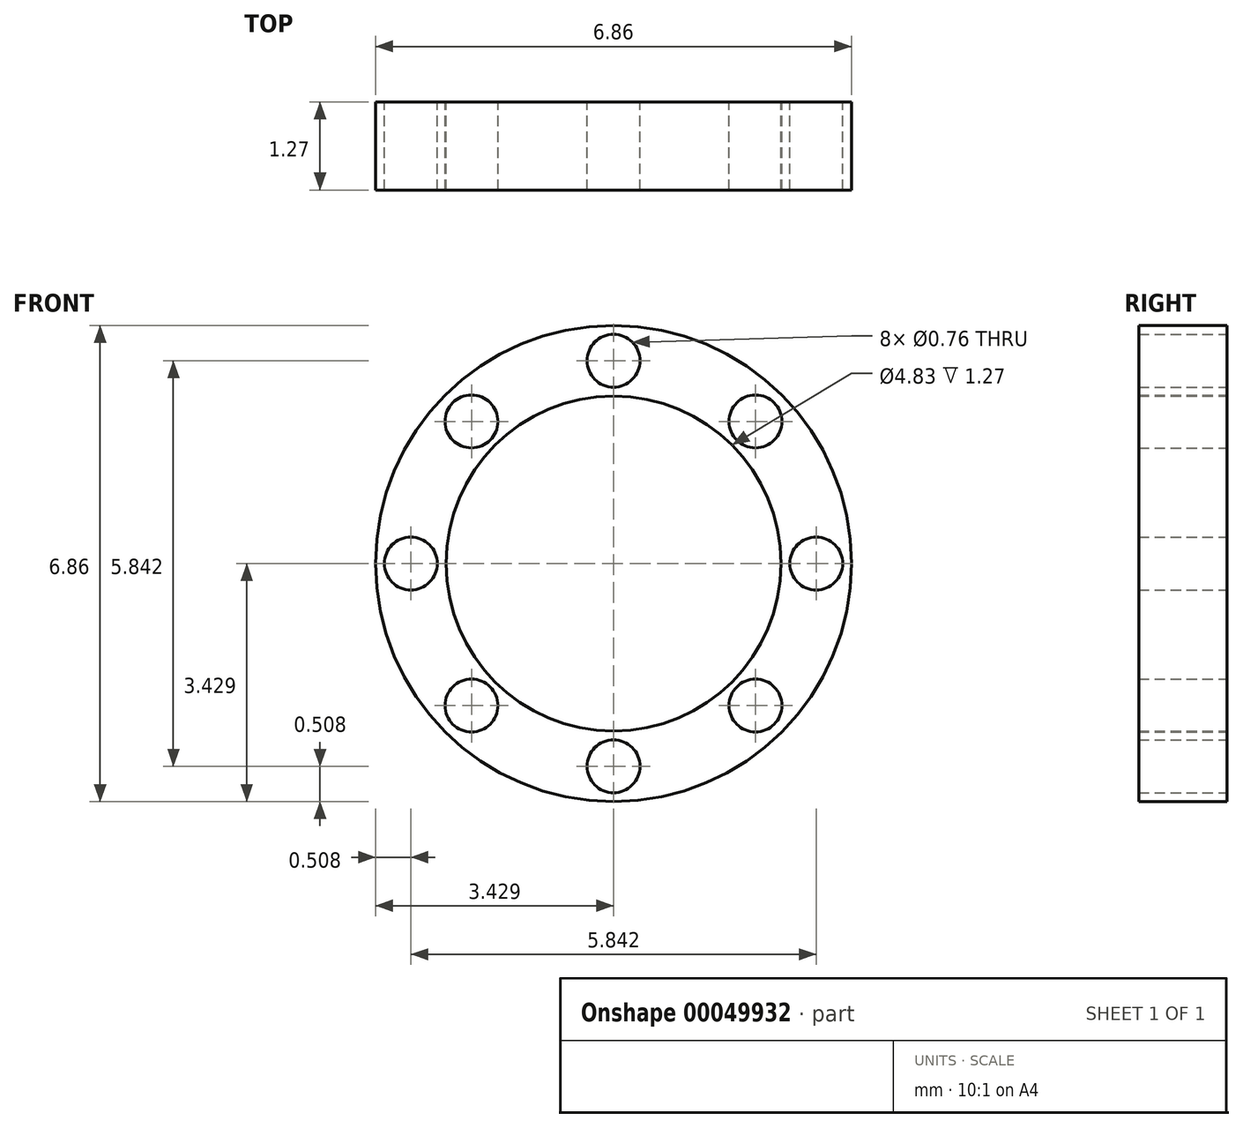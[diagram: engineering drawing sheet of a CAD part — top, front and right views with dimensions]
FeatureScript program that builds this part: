
annotation { "Feature Type Name" : "Feature", "Feature Type Description" : "" }
export const myFeature = defineFeature(function(context is Context, id is Id, definition is map)
    precondition{}
    {
        {
            var Q0;
            Q0=qCreatedBy(makeId("Front.planeOp"),FACE);
            var sketch = newSketch(context, id + "F0", { "sketchPlane" : qUnion([Q0])});
            skLineSegment(sketch, "E0", {"start": v(0, 0) * mm, "end": v(6.86, 0) * mm, "construction": true});
            skLineSegment(sketch, "E1", {"start": v(6.86, 0) * mm, "end": v(6.86, 6.86) * mm, "construction": true});
            skLineSegment(sketch, "E2", {"start": v(6.86, 6.86) * mm, "end": v(0, 6.86) * mm, "construction": true});
            skLineSegment(sketch, "E3", {"start": v(0, 6.86) * mm, "end": v(0, 0) * mm, "construction": true});
            skCircle(sketch, "E4", {"center": v(3.43, 3.43) * mm, "radius": 3.43 * mm});
            skLineSegment(sketch, "E5", {"start": v(3.43, 3.43) * mm, "end": v(1.02, 3.43) * mm});
            skCircle(sketch, "E6", {"center": v(3.43, 3.43) * mm, "radius": 2.41 * mm});
            skLineSegment(sketch, "E7", {"start": v(1.02, 3.43) * mm, "end": v(0, 3.43) * mm, "construction": true});
            skLineSegment(sketch, "E8", {"start": v(3.43, 6.86) * mm, "end": v(3.43, 0) * mm, "construction": true});
            skLineSegment(sketch, "E9", {"start": v(0, 6.86) * mm, "end": v(6.86, 0) * mm, "construction": true});
            skLineSegment(sketch, "E10", {"start": v(6.86, 6.86) * mm, "end": v(0, 0) * mm, "construction": true});
            skLineSegment(sketch, "E11", {"start": v(6.86, 0) * mm, "end": v(5.48, 1.38) * mm});
            skLineSegment(sketch, "E12", {"start": v(0, 6.86) * mm, "end": v(1.38, 5.48) * mm});
            skLineSegment(sketch, "E13", {"start": v(6.86, 6.86) * mm, "end": v(5.48, 5.48) * mm});
            skLineSegment(sketch, "E14", {"start": v(0, 0) * mm, "end": v(1.38, 1.38) * mm});
            skLineSegment(sketch, "E15", {"start": v(0, 3.43) * mm, "end": v(0.5, 3.43) * mm});
            skLineSegment(sketch, "E16", {"start": v(6.86, 3.43) * mm, "end": v(6.35, 3.43) * mm});
            skLineSegment(sketch, "E17", {"start": v(0.5, 3.43) * mm, "end": v(0.5, 3.05) * mm});
            skLineSegment(sketch, "E18", {"start": v(6.35, 3.43) * mm, "end": v(6.35, 3.05) * mm});
            skLineSegment(sketch, "E19", {"start": v(5.48, 1.38) * mm, "end": v(5.74, 1.65) * mm});
            skLineSegment(sketch, "E20", {"start": v(1.38, 1.38) * mm, "end": v(1.11, 1.65) * mm});
            skLineSegment(sketch, "E21", {"start": v(1.38, 5.48) * mm, "end": v(1.65, 5.74) * mm});
            skLineSegment(sketch, "E22", {"start": v(5.48, 5.48) * mm, "end": v(5.2, 5.74) * mm});
            skLineSegment(sketch, "E23", {"start": v(3.43, 6.86) * mm, "end": v(3.43, 6.35) * mm});
            skLineSegment(sketch, "E24", {"start": v(3.43, 6.35) * mm, "end": v(3.05, 6.35) * mm});
            skLineSegment(sketch, "E25", {"start": v(3.43, 0) * mm, "end": v(3.43, 0.5) * mm});
            skLineSegment(sketch, "E26", {"start": v(3.43, 0.5) * mm, "end": v(3.81, 0.5) * mm});
            skCircle(sketch, "E27", {"center": v(0.5, 3.43) * mm, "radius": 0.38 * mm});
            skCircle(sketch, "E28", {"center": v(1.38, 5.48) * mm, "radius": 0.38 * mm});
            skCircle(sketch, "E29", {"center": v(3.43, 6.35) * mm, "radius": 0.38 * mm});
            skCircle(sketch, "E30", {"center": v(5.48, 5.48) * mm, "radius": 0.38 * mm});
            skCircle(sketch, "E31", {"center": v(6.35, 3.43) * mm, "radius": 0.38 * mm});
            skCircle(sketch, "E32", {"center": v(5.48, 1.38) * mm, "radius": 0.38 * mm});
            skCircle(sketch, "E33", {"center": v(3.43, 0.5) * mm, "radius": 0.38 * mm});
            skCircle(sketch, "E34", {"center": v(1.38, 1.38) * mm, "radius": 0.38 * mm});
            skSolve(sketch);
        }
        {
            var Q0;
            Q0 = qSketchRegion(id + "F0", true);
            extrude(context, id + "F1", {"entities" : qUnion([Q0]), "depth" : 1.27 * mm});
        }
    });
